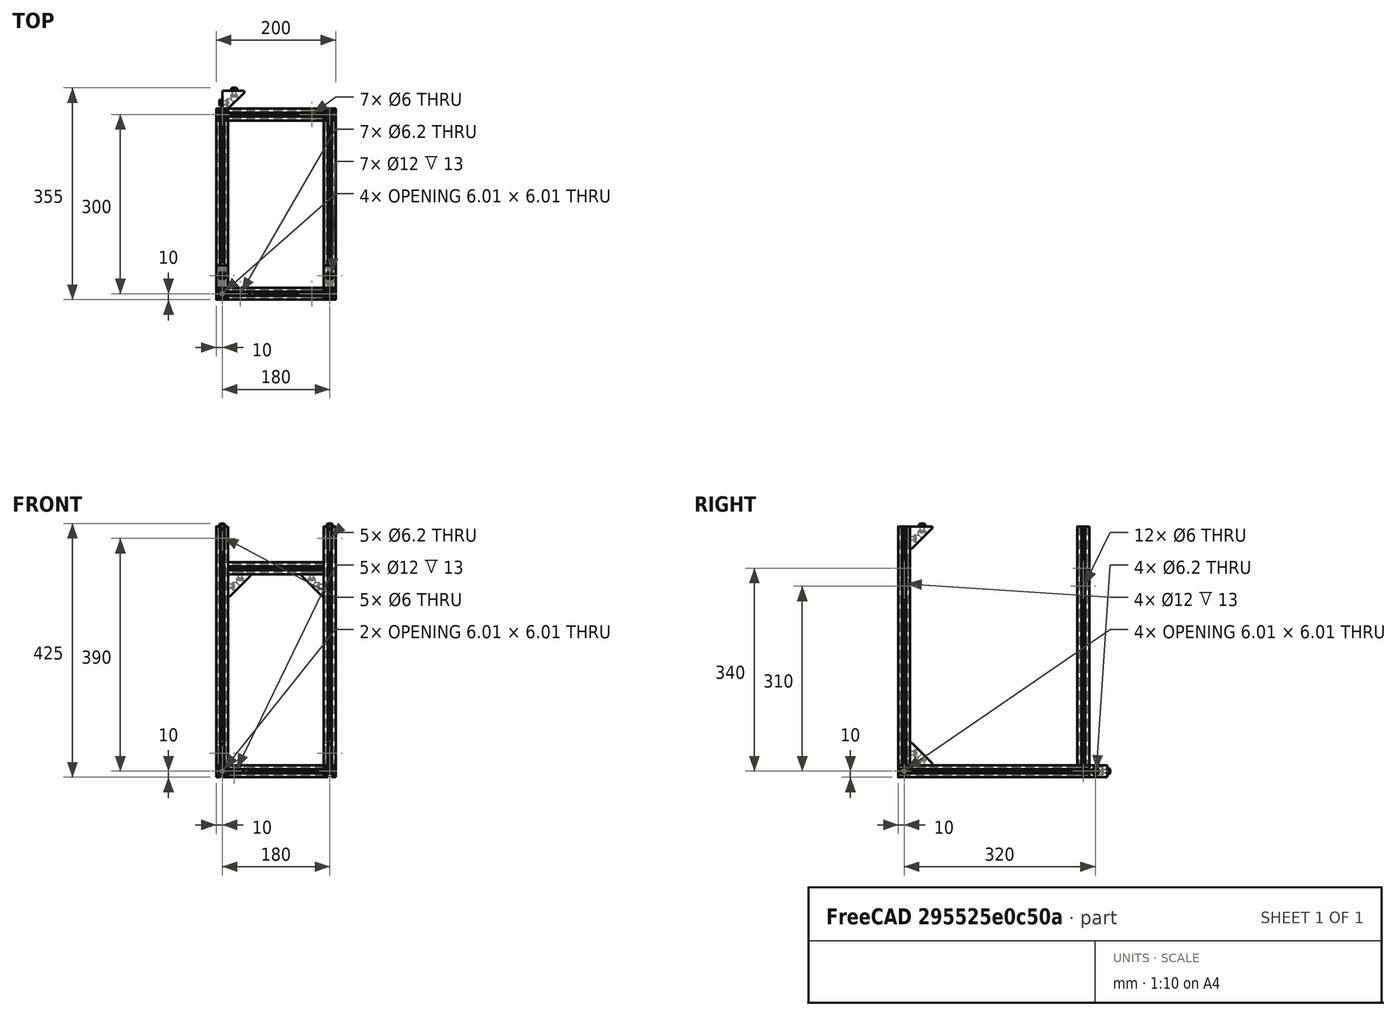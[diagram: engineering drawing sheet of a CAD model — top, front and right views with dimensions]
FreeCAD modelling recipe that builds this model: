
FCSTD DOCUMENT  (FreeCAD 0.17R9796 (Git))
Label: UPKframeNG2
License: All rights reserved
LicenseURL: http://en.wikipedia.org/wiki/All_rights_reserved
objects: Part::Feature×64, Part::FeaturePython×18, App::Part×7, Part::Compound×7
note: 89 computed .brp shape members not serialized (recipe doc carries the construction recipe); baked Part::Feature solids carry a one-line shape summary decoded from their .brp

FEATURE [Part::Feature] Pocket001001  label="tslot40"
  Placement = pos=(0,0,20) rot=(0,0,1;0rad)
  shape: bbox 20 x 20 x 400 mm, 94 faces (baked)
FEATURE [Part::Feature] Pocket003001  label="tslot32con"
  Placement = pos=(0,10,10) rot=(1,0,0;1.5708rad)
  shape: bbox 20 x 320 x 20 mm, 150 faces (baked)
FEATURE [Part::Feature] Pocket003002  label="tslot16"
  Placement = pos=(10,0,10) rot=(0,1,0;1.5708rad)
  shape: bbox 160 x 20 x 20 mm, 94 faces (baked)
FEATURE [Part::Feature] Pocket003006  label="tslot16_001"
  Placement = pos=(10,-300,10) rot=(0,1,0;1.5708rad)
  shape: bbox 160 x 20 x 20 mm, 94 faces (baked)
FEATURE [Part::Feature] Pocket003007  label="tslot32con_001"
  Placement = pos=(180,-310,10) rot=(0,0.707107,0.707107;3.14159rad)
  shape: bbox 20 x 320 x 20 mm, 150 faces (baked)
FEATURE [Part::FeaturePython] Screw  label="M6x25-Screw"  # Fasteners workbench fastener (typed FeaturePython)
  Placement = pos=(-4,0,10) rot=(0,-1,0;1.5708rad)
  diameter = 7
  invert = false
  length = 6
  matchOuter = false
  offset = 0
  thread = false
  type = 15
FEATURE [Part::FeaturePython] Screw001  label="M6x25-Screw004"  # Fasteners workbench fastener (typed FeaturePython)
  Placement = pos=(-4,-300,10) rot=(0,-1,0;1.5708rad)
  diameter = 7
  invert = false
  length = 6
  matchOuter = false
  offset = 0
  thread = false
  type = 15
FEATURE [Part::FeaturePython] Screw002  label="M6x25-Screw005"  # Fasteners workbench fastener (typed FeaturePython)
  Placement = pos=(184,0,10) rot=(0,1,0;1.5708rad)
  diameter = 7
  invert = false
  length = 6
  matchOuter = false
  offset = 0
  thread = false
  type = 15
FEATURE [Part::FeaturePython] Screw004  label="M6x25-Screw006"  # Fasteners workbench fastener (typed FeaturePython)
  Placement = pos=(184,-300,10) rot=(0,1,0;1.5708rad)
  diameter = 7
  invert = false
  length = 6
  matchOuter = false
  offset = 0
  thread = false
  type = 15
FEATURE [App::Part] Part  label="lower_frame"
  Group = -> [Pocket003001,Pocket003002,Pocket003006,Pocket003007,Screw,Screw001,Screw002,Screw004]
  License = CC BY 3.0
  LicenseURL = http://creativecommons.org/licenses/by/3.0/
  Origin = -> PartOrigin
FEATURE [Part::Feature] Pocket003008  label="tslot32con001"
  Placement = pos=(0,10,10) rot=(1,0,0;1.5708rad)
  shape: bbox 20 x 320 x 20 mm, 150 faces (baked)
FEATURE [Part::Feature] Pocket003009  label="tslot041"
  Placement = pos=(10,0,10) rot=(0,1,0;1.5708rad)
  shape: bbox 160 x 20 x 20 mm, 94 faces (baked)
FEATURE [Part::Feature] Pocket003010  label="tslot16_002"
  Placement = pos=(10,-300,10) rot=(0,1,0;1.5708rad)
  shape: bbox 160 x 20 x 20 mm, 94 faces (baked)
FEATURE [Part::Feature] Pocket003011  label="tslot32con_002"
  Placement = pos=(180,-310,10) rot=(0,0.707107,0.707107;3.14159rad)
  shape: bbox 20 x 320 x 20 mm, 150 faces (baked)
FEATURE [Part::FeaturePython] Screw005  label="M6x25-Screw007"  # Fasteners workbench fastener (typed FeaturePython)
  Placement = pos=(-4,0,10) rot=(0,-1,0;1.5708rad)
  diameter = 7
  invert = false
  length = 6
  matchOuter = false
  offset = 0
  thread = false
  type = 15
FEATURE [Part::FeaturePython] Screw006  label="M6x25-Screw008"  # Fasteners workbench fastener (typed FeaturePython)
  Placement = pos=(-4,-300,10) rot=(0,-1,0;1.5708rad)
  diameter = 7
  invert = false
  length = 6
  matchOuter = false
  offset = 0
  thread = false
  type = 15
FEATURE [Part::FeaturePython] Screw007  label="M6x25-Screw009"  # Fasteners workbench fastener (typed FeaturePython)
  Placement = pos=(184,0,10) rot=(0,1,0;1.5708rad)
  diameter = 7
  invert = false
  length = 6
  matchOuter = false
  offset = 0
  thread = false
  type = 15
FEATURE [Part::FeaturePython] Screw008  label="M6x25-Screw010"  # Fasteners workbench fastener (typed FeaturePython)
  Placement = pos=(184,-300,10) rot=(0,1,0;1.5708rad)
  diameter = 7
  invert = false
  length = 6
  matchOuter = false
  offset = 0
  thread = false
  type = 15
FEATURE [App::Part] Part001  label="upper_frame"
  Group = -> [Pocket003008,Pocket003009,Pocket003010,Pocket003011,Screw005,Screw006,Screw007,Screw008]
  License = CC BY 3.0
  LicenseURL = http://creativecommons.org/licenses/by/3.0/
  Origin = -> PartOrigin001
  Placement = pos=(0,0,420) rot=(0,0,1;0rad)
FEATURE [Part::Feature] Pocket003012  label="tslot042"
  Placement = pos=(180,0,20) rot=(0,0,1;0rad)
  shape: bbox 20 x 20 x 400 mm, 94 faces (baked)
FEATURE [Part::Feature] Pocket003013  label="tslot043"
  Placement = pos=(180,-300,20) rot=(0,0,1;0rad)
  shape: bbox 20 x 20 x 400 mm, 94 faces (baked)
FEATURE [Part::Feature] Pocket003014  label="tslot044"
  Placement = pos=(0,-300,20) rot=(0,0,1;0rad)
  shape: bbox 20 x 20 x 400 mm, 94 faces (baked)
FEATURE [Part::Feature] Fillet004001  label="Fillet005"
  shape: bbox 37.5 x 37.5 x 20 mm, 26 faces (baked)
FEATURE [Part::FeaturePython] Screw009  label="M6x12-Screw"  # Fasteners workbench fastener (typed FeaturePython)
  Placement = pos=(7,20,10) rot=(0,1,0;1.5708rad)
  diameter = 4
  invert = false
  length = 1
  matchOuter = false
  offset = 0
  thread = false
  type = 20
FEATURE [Part::Feature] Body001  label="m6nutplate"
  Placement = pos=(-1.5,15,5) rot=(0,-1,0;1.5708rad)
  shape: bbox 3 x 10 x 10 mm, 9 faces (baked)
FEATURE [Part::FeaturePython] Screw010  label="M6x12-Screw001"  # Fasteners workbench fastener (typed FeaturePython)
  Placement = pos=(20,33,10) rot=(1,0,0;1.5708rad)
  diameter = 4
  invert = false
  length = 1
  matchOuter = false
  offset = 0
  thread = false
  type = 20
FEATURE [Part::Feature] Body002  label="m6nutplate001"
  Placement = pos=(15,41.5,5) rot=(0.57735,0.57735,0.57735;4.18879rad)
  shape: bbox 10 x 3 x 10 mm, 9 faces (baked)
FEATURE [App::Part] Part002  label="cornerstonescrewnut"
  Group = -> [Body001,Screw009,Fillet004001,Screw010,Body002]
  License = CC BY 3.0
  LicenseURL = http://creativecommons.org/licenses/by/3.0/
  Origin = -> PartOrigin002
  Placement = pos=(10,-50,20) rot=(0,-1,0;1.5708rad)
FEATURE [Part::Feature] Fillet004002  label="Fillet006"
  shape: bbox 37.5 x 37.5 x 20 mm, 26 faces (baked)
FEATURE [Part::FeaturePython] Screw011  label="M6x12-Screw002"  # Fasteners workbench fastener (typed FeaturePython)
  Placement = pos=(7,20,10) rot=(0,1,0;1.5708rad)
  diameter = 4
  invert = false
  length = 1
  matchOuter = false
  offset = 0
  thread = false
  type = 20
FEATURE [Part::Feature] Body003  label="m6nutplate002"
  Placement = pos=(-1.5,15,5) rot=(0,-1,0;1.5708rad)
  shape: bbox 3 x 10 x 10 mm, 9 faces (baked)
FEATURE [Part::FeaturePython] Screw012  label="M6x12-Screw003"  # Fasteners workbench fastener (typed FeaturePython)
  Placement = pos=(20,33,10) rot=(1,0,0;1.5708rad)
  diameter = 4
  invert = false
  length = 1
  matchOuter = false
  offset = 0
  thread = false
  type = 20
FEATURE [Part::Feature] Body004  label="m6nutplate003"
  Placement = pos=(15,41.5,5) rot=(0.57735,0.57735,0.57735;4.18879rad)
  shape: bbox 10 x 3 x 10 mm, 9 faces (baked)
FEATURE [App::Part] Part003  label="cornerstonescrewnut001"
  Group = -> [Body003,Screw011,Fillet004002,Screw012,Body004]
  License = CC BY 3.0
  LicenseURL = http://creativecommons.org/licenses/by/3.0/
  Origin = -> PartOrigin003
  Placement = pos=(190,-50,20) rot=(0,-1,0;1.5708rad)
FEATURE [Part::Feature] Fillet004003  label="Fillet007"
  shape: bbox 37.5 x 37.5 x 20 mm, 26 faces (baked)
FEATURE [Part::FeaturePython] Screw013  label="M6x12-Screw004"  # Fasteners workbench fastener (typed FeaturePython)
  Placement = pos=(7,20,10) rot=(0,1,0;1.5708rad)
  diameter = 4
  invert = false
  length = 1
  matchOuter = false
  offset = 0
  thread = false
  type = 20
FEATURE [Part::Feature] Body005  label="m6nutplate004"
  Placement = pos=(-1.5,15,5) rot=(0,-1,0;1.5708rad)
  shape: bbox 3 x 10 x 10 mm, 9 faces (baked)
FEATURE [Part::FeaturePython] Screw014  label="M6x12-Screw005"  # Fasteners workbench fastener (typed FeaturePython)
  Placement = pos=(20,33,10) rot=(1,0,0;1.5708rad)
  diameter = 4
  invert = false
  length = 1
  matchOuter = false
  offset = 0
  thread = false
  type = 20
FEATURE [Part::Feature] Body006  label="m6nutplate005"
  Placement = pos=(15,41.5,5) rot=(0.57735,0.57735,0.57735;4.18879rad)
  shape: bbox 10 x 3 x 10 mm, 9 faces (baked)
FEATURE [App::Part] Part004  label="cornerstonescrewnut002"
  Group = -> [Body005,Screw013,Fillet004003,Screw014,Body006]
  License = CC BY 3.0
  LicenseURL = http://creativecommons.org/licenses/by/3.0/
  Origin = -> PartOrigin004
  Placement = pos=(-10,-50,420) rot=(0,1,0;1.5708rad)
FEATURE [Part::Feature] Fillet004004  label="Fillet008"
  shape: bbox 37.5 x 37.5 x 20 mm, 26 faces (baked)
FEATURE [Part::FeaturePython] Screw015  label="M6x12-Screw006"  # Fasteners workbench fastener (typed FeaturePython)
  Placement = pos=(7,20,10) rot=(0,1,0;1.5708rad)
  diameter = 4
  invert = false
  length = 1
  matchOuter = false
  offset = 0
  thread = false
  type = 20
FEATURE [Part::Feature] Body007  label="m6nutplate006"
  Placement = pos=(-1.5,15,5) rot=(0,-1,0;1.5708rad)
  shape: bbox 3 x 10 x 10 mm, 9 faces (baked)
FEATURE [Part::FeaturePython] Screw016  label="M6x12-Screw007"  # Fasteners workbench fastener (typed FeaturePython)
  Placement = pos=(20,33,10) rot=(1,0,0;1.5708rad)
  diameter = 4
  invert = false
  length = 1
  matchOuter = false
  offset = 0
  thread = false
  type = 20
FEATURE [Part::Feature] Body008  label="m6nutplate007"
  Placement = pos=(15,41.5,5) rot=(0.57735,0.57735,0.57735;4.18879rad)
  shape: bbox 10 x 3 x 10 mm, 9 faces (baked)
FEATURE [App::Part] Part005  label="cornerstonescrewnut003"
  Group = -> [Body007,Screw015,Fillet004004,Screw016,Body008]
  License = CC BY 3.0
  LicenseURL = http://creativecommons.org/licenses/by/3.0/
  Origin = -> PartOrigin005
  Placement = pos=(170,-50,420) rot=(0,1,0;1.5708rad)
FEATURE [Part::Feature] Fillet004005  label="Fillet009"
  shape: bbox 37.5 x 37.5 x 20 mm, 26 faces (baked)
FEATURE [Part::FeaturePython] Screw017  label="M6x12-Screw008"  # Fasteners workbench fastener (typed FeaturePython)
  Placement = pos=(7,20,10) rot=(0,1,0;1.5708rad)
  diameter = 4
  invert = false
  length = 1
  matchOuter = false
  offset = 0
  thread = false
  type = 20
FEATURE [Part::Feature] Body009  label="m6nutplate008"
  Placement = pos=(-1.5,15,5) rot=(0,-1,0;1.5708rad)
  shape: bbox 3 x 10 x 10 mm, 9 faces (baked)
FEATURE [Part::FeaturePython] Screw018  label="M6x12-Screw009"  # Fasteners workbench fastener (typed FeaturePython)
  Placement = pos=(20,33,10) rot=(1,0,0;1.5708rad)
  diameter = 4
  invert = false
  length = 1
  matchOuter = false
  offset = 0
  thread = false
  type = 20
FEATURE [Part::Feature] Body010  label="m6nutplate009"
  Placement = pos=(15,41.5,5) rot=(0.57735,0.57735,0.57735;4.18879rad)
  shape: bbox 10 x 3 x 10 mm, 9 faces (baked)
FEATURE [App::Part] Part006  label="cornerstonescrewnut004"
  Group = -> [Body009,Screw017,Fillet004005,Screw018,Body010]
  License = CC BY 3.0
  LicenseURL = http://creativecommons.org/licenses/by/3.0/
  Origin = -> PartOrigin006
  Placement = pos=(10,10,300) rot=(1,0,0;1.5708rad)
FEATURE [Part::Feature] Body009001  label="m6nutplate010"
  Placement = pos=(-1.5,15,5) rot=(0,-1,0;1.5708rad)
  shape: bbox 3 x 10 x 10 mm, 9 faces (baked)
FEATURE [Part::Feature] Body010001  label="m6nutplate011"
  Placement = pos=(15,41.5,5) rot=(0.57735,0.57735,0.57735;4.18879rad)
  shape: bbox 10 x 3 x 10 mm, 9 faces (baked)
FEATURE [Part::Feature] Screw018001  label="M6x12-Screw010"
  Placement = pos=(20,33,10) rot=(1,0,0;1.5708rad)
  shape: bbox 10.5 x 15.3 x 10.5 mm, 15 faces (baked)
FEATURE [Part::Feature] Screw017001  label="M6x12-Screw011"
  Placement = pos=(7,20,10) rot=(0,1,0;1.5708rad)
  shape: bbox 15.3 x 10.5 x 10.5 mm, 15 faces (baked)
FEATURE [Part::Feature] Fillet004005001  label="Fillet010"
  shape: bbox 37.5 x 37.5 x 20 mm, 26 faces (baked)
FEATURE [Part::Compound] Compound
  Links = -> [Body009001,Fillet004005001,Screw017001,Body010001,Screw018001]
  Placement = pos=(10,-250,420) rot=(0.707107,0,-0.707107;3.14159rad)
FEATURE [Part::Feature] Body010002  label="m6nutplate012"
  Placement = pos=(-1.5,15,5) rot=(0,-1,0;1.5708rad)
  shape: bbox 3 x 10 x 10 mm, 9 faces (baked)
FEATURE [Part::Feature] Body010003  label="m6nutplate013"
  Placement = pos=(15,41.5,5) rot=(0.57735,0.57735,0.57735;4.18879rad)
  shape: bbox 10 x 3 x 10 mm, 9 faces (baked)
FEATURE [Part::Feature] Screw018002  label="M6x12-Screw012"
  Placement = pos=(20,33,10) rot=(1,0,0;1.5708rad)
  shape: bbox 10.5 x 15.3 x 10.5 mm, 15 faces (baked)
FEATURE [Part::Feature] Screw018003  label="M6x12-Screw013"
  Placement = pos=(7,20,10) rot=(0,1,0;1.5708rad)
  shape: bbox 15.3 x 10.5 x 10.5 mm, 15 faces (baked)
FEATURE [Part::Feature] Fillet004005002  label="Fillet011"
  shape: bbox 37.5 x 37.5 x 20 mm, 26 faces (baked)
FEATURE [Part::Compound] Compound001
  Links = -> [Body010002,Fillet004005002,Screw018003,Body010003,Screw018002]
  Placement = pos=(190,-250,420) rot=(0.707107,0,-0.707107;3.14159rad)
FEATURE [Part::Feature] Body010004  label="m6nutplate014"
  Placement = pos=(-1.5,15,5) rot=(0,-1,0;1.5708rad)
  shape: bbox 3 x 10 x 10 mm, 9 faces (baked)
FEATURE [Part::Feature] Body010005  label="m6nutplate015"
  Placement = pos=(15,41.5,5) rot=(0.57735,0.57735,0.57735;4.18879rad)
  shape: bbox 10 x 3 x 10 mm, 9 faces (baked)
FEATURE [Part::Feature] Screw018004  label="M6x12-Screw014"
  Placement = pos=(20,33,10) rot=(1,0,0;1.5708rad)
  shape: bbox 10.5 x 15.3 x 10.5 mm, 15 faces (baked)
FEATURE [Part::Feature] Screw018005  label="M6x12-Screw015"
  Placement = pos=(7,20,10) rot=(0,1,0;1.5708rad)
  shape: bbox 15.3 x 10.5 x 10.5 mm, 15 faces (baked)
FEATURE [Part::Feature] Fillet004005003  label="Fillet012"
  shape: bbox 37.5 x 37.5 x 20 mm, 26 faces (baked)
FEATURE [Part::Compound] Compound002
  Links = -> [Body010004,Fillet004005003,Screw018005,Body010005,Screw018004]
  Placement = pos=(10,-290,60) rot=(0.57735,0.57735,-0.57735;4.18879rad)
FEATURE [Part::Feature] Body010006  label="m6nutplate016"
  Placement = pos=(-1.5,15,5) rot=(0,-1,0;1.5708rad)
  shape: bbox 3 x 10 x 10 mm, 9 faces (baked)
FEATURE [Part::Feature] Body010007  label="m6nutplate017"
  Placement = pos=(15,41.5,5) rot=(0.57735,0.57735,0.57735;4.18879rad)
  shape: bbox 10 x 3 x 10 mm, 9 faces (baked)
FEATURE [Part::Feature] Screw018006  label="M6x12-Screw016"
  Placement = pos=(20,33,10) rot=(1,0,0;1.5708rad)
  shape: bbox 10.5 x 15.3 x 10.5 mm, 15 faces (baked)
FEATURE [Part::Feature] Screw018007  label="M6x12-Screw017"
  Placement = pos=(7,20,10) rot=(0,1,0;1.5708rad)
  shape: bbox 15.3 x 10.5 x 10.5 mm, 15 faces (baked)
FEATURE [Part::Feature] Fillet004005004  label="Fillet013"
  shape: bbox 37.5 x 37.5 x 20 mm, 26 faces (baked)
FEATURE [Part::Compound] Compound003
  Links = -> [Body010006,Fillet004005004,Screw018007,Body010007,Screw018006]
  Placement = pos=(190,-290,60) rot=(0.57735,0.57735,-0.57735;4.18879rad)
FEATURE [Part::Feature] Pocket003015  label="tslot16_across"
  Placement = pos=(10,0,350) rot=(0,1,0;1.5708rad)
  shape: bbox 160 x 20 x 20 mm, 94 faces (baked)
FEATURE [Part::Feature] Pocket003016  label="tslot16_across001"
  Placement = pos=(10,-300,350) rot=(0,1,0;1.5708rad)
  shape: bbox 160 x 20 x 20 mm, 94 faces (baked)
FEATURE [Part::Feature] Body010008  label="m6nutplate018"
  Placement = pos=(-1.5,15,5) rot=(0,-1,0;1.5708rad)
  shape: bbox 3 x 10 x 10 mm, 9 faces (baked)
FEATURE [Part::Feature] Body010009  label="m6nutplate019"
  Placement = pos=(15,41.5,5) rot=(0.57735,0.57735,0.57735;4.18879rad)
  shape: bbox 10 x 3 x 10 mm, 9 faces (baked)
FEATURE [Part::Feature] Screw018008  label="M6x12-Screw018"
  Placement = pos=(20,33,10) rot=(1,0,0;1.5708rad)
  shape: bbox 10.5 x 15.3 x 10.5 mm, 15 faces (baked)
FEATURE [Part::Feature] Screw018009  label="M6x12-Screw019"
  Placement = pos=(7,20,10) rot=(0,1,0;1.5708rad)
  shape: bbox 15.3 x 10.5 x 10.5 mm, 15 faces (baked)
FEATURE [Part::Feature] Fillet004005005  label="Fillet014"
  shape: bbox 37.5 x 37.5 x 20 mm, 26 faces (baked)
FEATURE [Part::Compound] Compound004
  Links = -> [Body010008,Fillet004005005,Screw018009,Body010009,Screw018008]
  Placement = pos=(10,-290,300) rot=(1,0,0;1.5708rad)
FEATURE [Part::Feature] Body010010  label="m6nutplate020"
  Placement = pos=(-1.5,15,5) rot=(0,-1,0;1.5708rad)
  shape: bbox 3 x 10 x 10 mm, 9 faces (baked)
FEATURE [Part::Feature] Body010011  label="m6nutplate021"
  Placement = pos=(15,41.5,5) rot=(0.57735,0.57735,0.57735;4.18879rad)
  shape: bbox 10 x 3 x 10 mm, 9 faces (baked)
FEATURE [Part::Feature] Screw018010  label="M6x12-Screw020"
  Placement = pos=(20,33,10) rot=(1,0,0;1.5708rad)
  shape: bbox 10.5 x 15.3 x 10.5 mm, 15 faces (baked)
FEATURE [Part::Feature] Screw018011  label="M6x12-Screw021"
  Placement = pos=(7,20,10) rot=(0,1,0;1.5708rad)
  shape: bbox 15.3 x 10.5 x 10.5 mm, 15 faces (baked)
FEATURE [Part::Feature] Fillet004005006  label="Fillet015"
  shape: bbox 37.5 x 37.5 x 20 mm, 26 faces (baked)
FEATURE [Part::Compound] Compound005
  Links = -> [Body010010,Fillet004005006,Screw018011,Body010011,Screw018010]
  Placement = pos=(130,-290,340) rot=(0.57735,0.57735,-0.57735;2.0944rad)
FEATURE [Part::Feature] Body010012  label="m6nutplate022"
  Placement = pos=(-1.5,15,5) rot=(0,-1,0;1.5708rad)
  shape: bbox 3 x 10 x 10 mm, 9 faces (baked)
FEATURE [Part::Feature] Body010013  label="m6nutplate023"
  Placement = pos=(15,41.5,5) rot=(0.57735,0.57735,0.57735;4.18879rad)
  shape: bbox 10 x 3 x 10 mm, 9 faces (baked)
FEATURE [Part::Feature] Screw018012  label="M6x12-Screw022"
  Placement = pos=(20,33,10) rot=(1,0,0;1.5708rad)
  shape: bbox 10.5 x 15.3 x 10.5 mm, 15 faces (baked)
FEATURE [Part::Feature] Screw018013  label="M6x12-Screw023"
  Placement = pos=(7,20,10) rot=(0,1,0;1.5708rad)
  shape: bbox 15.3 x 10.5 x 10.5 mm, 15 faces (baked)
FEATURE [Part::Feature] Fillet004005007  label="Fillet016"
  shape: bbox 37.5 x 37.5 x 20 mm, 26 faces (baked)
FEATURE [Part::Compound] Compound006
  Links = -> [Body010012,Fillet004005007,Screw018013,Body010013,Screw018012]
  Placement = pos=(130,10,340) rot=(0.57735,0.57735,-0.57735;2.0944rad)
